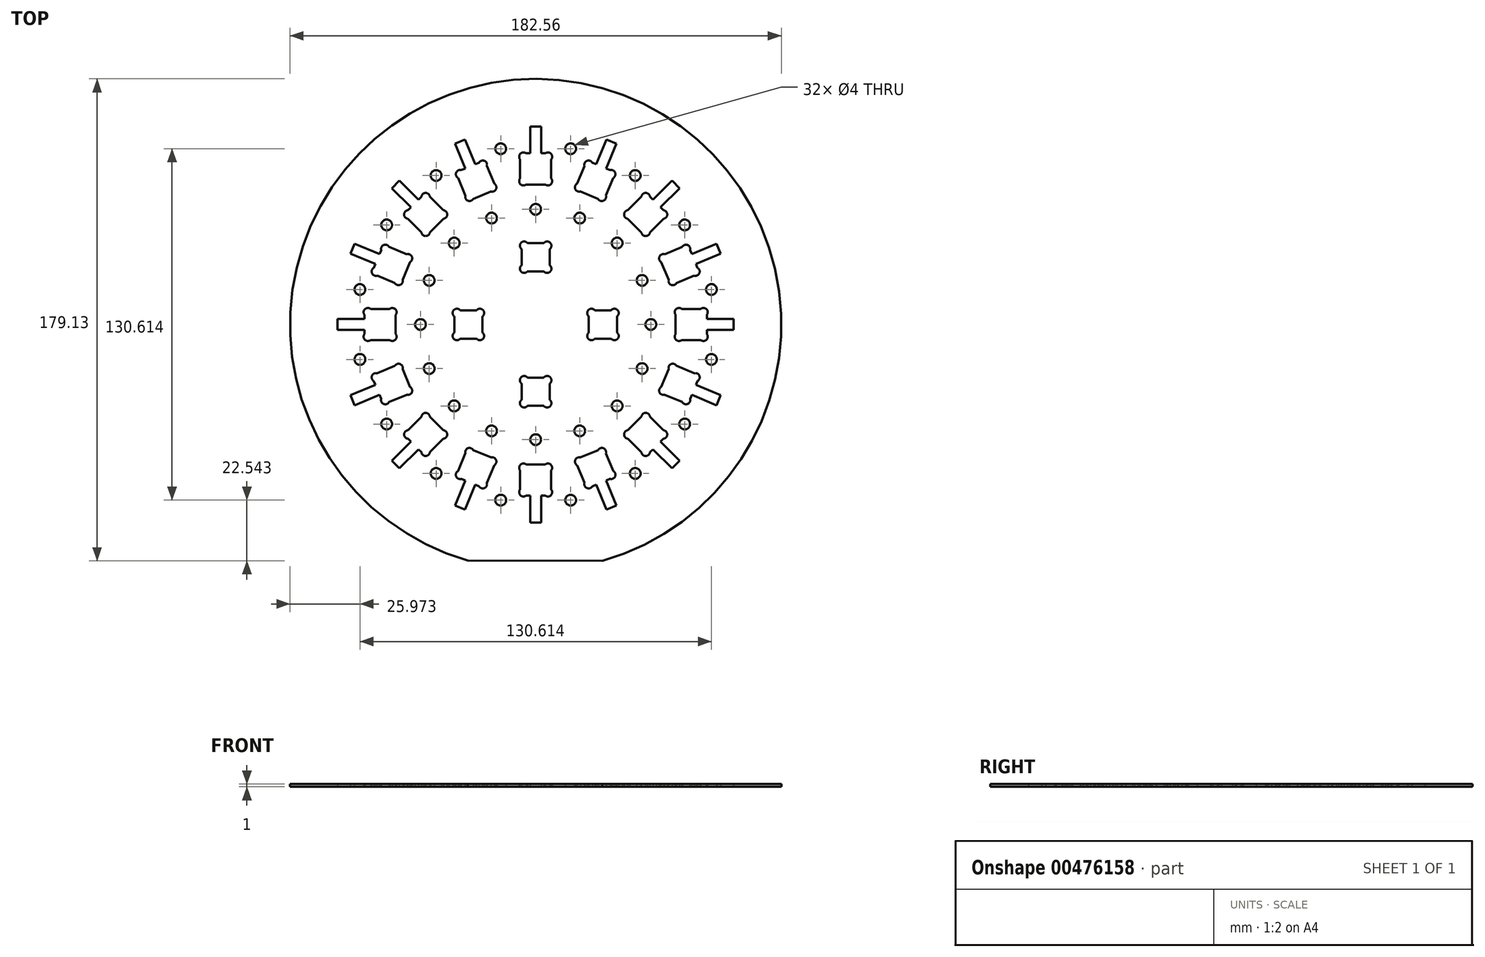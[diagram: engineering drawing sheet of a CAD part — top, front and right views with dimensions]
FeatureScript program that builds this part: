
annotation { "Feature Type Name" : "Feature", "Feature Type Description" : "" }
export const myFeature = defineFeature(function(context is Context, id is Id, definition is map)
    precondition{}
    {
        {
            var Q0;
            Q0=qCreatedBy(makeId("Top.planeOp"),FACE);
            var sketch = newSketch(context, id + "F0", { "sketchPlane" : qUnion([Q0])});
            skArc(sketch, "E0", {"start": v(24.78, -87.85) * mm, "mid": v(0.23, 91.28) * mm, "end": v(-25.22, -87.73) * mm});
            skLineSegment(sketch, "E1", {"start": v(-25.22, -87.73) * mm, "end": v(24.78, -87.85) * mm});
            skLineSegment(sketch, "E2", {"start": v(0, 0) * mm, "end": v(-0.22, -87.8) * mm, "construction": true});
            skLineSegment(sketch, "E3.bottom", {"start": v(5.8, 52) * mm, "end": v(3.57, 52) * mm, "construction": true});
            skLineSegment(sketch, "E3.top", {"start": v(5.8, 63.6) * mm, "end": v(3.57, 63.6) * mm, "construction": true});
            skLineSegment(sketch, "E3.left", {"start": v(5.8, 52) * mm, "end": v(5.8, 52) * mm});
            skLineSegment(sketch, "E3.right", {"start": v(-5.8, 52) * mm, "end": v(-5.8, 54.24) * mm, "construction": true});
            skPoint(sketch, "E3.middle", {"position": v(0, 57.8) * mm});
            skLineSegment(sketch, "E4", {"start": v(0, 57.8) * mm, "end": v(5.8, 63.6) * mm, "construction": true});
            skLineSegment(sketch, "E5", {"start": v(5.8, 63.6) * mm, "end": v(5.61, 63.54) * mm, "construction": true});
            skArc(sketch, "E6", {"start": v(5.8, 61.38) * mm, "mid": v(5.67, 63.48) * mm, "end": v(3.57, 63.6) * mm});
            skArc(sketch, "E7", {"start": v(3.57, 63.6) * mm, "mid": v(3.43, 61.23) * mm, "end": v(5.8, 61.38) * mm, "construction": true});
            skLineSegment(sketch, "E8", {"start": v(5.8, 61.38) * mm, "end": v(5.8, 63.6) * mm, "construction": true});
            skLineSegment(sketch, "E9", {"start": v(5.8, 52) * mm, "end": v(5.8, 54.24) * mm, "construction": true});
            skLineSegment(sketch, "E10", {"start": v(3.57, 63.6) * mm, "end": v(3.57, 63.6) * mm});
            skLineSegment(sketch, "E11", {"start": v(-5.8, 63.6) * mm, "end": v(-5.8, 63.6) * mm});
            skArc(sketch, "E12.1.0", {"start": v(-3.57, 63.6) * mm, "mid": v(-5.67, 63.48) * mm, "end": v(-5.8, 61.38) * mm});
            skArc(sketch, "E12.2.0", {"start": v(-5.8, 54.24) * mm, "mid": v(-5.67, 52.13) * mm, "end": v(-3.57, 52) * mm});
            skArc(sketch, "E13.2.3.0", {"start": v(3.57, 52) * mm, "mid": v(5.67, 52.13) * mm, "end": v(5.8, 54.24) * mm});
            skLineSegment(sketch, "E14", {"start": v(-5.8, 61.38) * mm, "end": v(-5.8, 63.6) * mm, "construction": true});
            skLineSegment(sketch, "E15", {"start": v(-5.8, 54.24) * mm, "end": v(-5.8, 61.38) * mm});
            skLineSegment(sketch, "E16", {"start": v(-3.57, 52) * mm, "end": v(-5.8, 52) * mm, "construction": true});
            skLineSegment(sketch, "E17", {"start": v(3.57, 52) * mm, "end": v(-3.57, 52) * mm});
            skLineSegment(sketch, "E18", {"start": v(3.57, 63.6) * mm, "end": v(-3.57, 63.6) * mm});
            skLineSegment(sketch, "E19", {"start": v(-3.57, 63.6) * mm, "end": v(-5.8, 63.6) * mm, "construction": true});
            skLineSegment(sketch, "E20", {"start": v(5.8, 54.24) * mm, "end": v(5.8, 61.38) * mm});
            skLineSegment(sketch, "E21", {"start": v(5.8, 61.38) * mm, "end": v(5.8, 61.38) * mm});
            skLineSegment(sketch, "E22", {"start": v(0, 57.8) * mm, "end": v(0, 42.8) * mm, "construction": true});
            skCircle(sketch, "E23", {"center": v(0, 42.8) * mm, "radius": 2 * mm});
            skCircle(sketch, "E24.1.0", {"center": v(13, 65.3) * mm, "radius": 2 * mm});
            skCircle(sketch, "E24.2.0", {"center": v(-13, 65.3) * mm, "radius": 2 * mm});
            skLineSegment(sketch, "E25.1.0", {"start": v(-26.11, 47.89) * mm, "end": v(-28.85, 54.49) * mm});
            skLineSegment(sketch, "E25.1.1", {"start": v(-16.6, 49.41) * mm, "end": v(-23.2, 46.68) * mm});
            skCircle(sketch, "E25.1.2", {"center": v(-16.38, 39.55) * mm, "radius": 2 * mm});
            skLineSegment(sketch, "E25.1.3", {"start": v(-22.12, 53.4) * mm, "end": v(-16.38, 39.55) * mm, "construction": true});
            skCircle(sketch, "E25.1.4", {"center": v(-37, 55.36) * mm, "radius": 2 * mm});
            skLineSegment(sketch, "E25.1.6", {"start": v(-15.4, 52.33) * mm, "end": v(-18.13, 58.93) * mm});
            skArc(sketch, "E25.1.7", {"start": v(-21.04, 60.13) * mm, "mid": v(-20.27, 57.89) * mm, "end": v(-18.13, 58.93) * mm, "construction": true});
            skPoint(sketch, "E25.1.8", {"position": v(-22.12, 53.4) * mm});
            skLineSegment(sketch, "E25.1.9", {"start": v(-22.12, 53.4) * mm, "end": v(-18.98, 60.98) * mm, "construction": true});
            skLineSegment(sketch, "E25.1.10", {"start": v(-21.04, 60.13) * mm, "end": v(-27.64, 57.4) * mm});
            skPoint(sketch, "E25.1.11", {"position": v(-22.12, 53.4) * mm});
            skArc(sketch, "E25.1.12", {"start": v(-26.11, 47.89) * mm, "mid": v(-25.2, 46) * mm, "end": v(-23.2, 46.68) * mm});
            skPoint(sketch, "E25.1.13", {"position": v(-22.12, 53.4) * mm});
            skLineSegment(sketch, "E25.1.14", {"start": v(-25.26, 45.83) * mm, "end": v(-26.11, 47.89) * mm, "construction": true});
            skLineSegment(sketch, "E25.1.15", {"start": v(-27.64, 57.4) * mm, "end": v(-29.7, 56.55) * mm, "construction": true});
            skArc(sketch, "E25.1.16", {"start": v(-27.64, 57.4) * mm, "mid": v(-29.53, 56.48) * mm, "end": v(-28.85, 54.49) * mm});
            skLineSegment(sketch, "E25.1.17", {"start": v(-14.54, 50.27) * mm, "end": v(-15.4, 52.33) * mm, "construction": true});
            skPoint(sketch, "E25.1.18", {"position": v(-22.12, 53.4) * mm});
            skLineSegment(sketch, "E25.1.19", {"start": v(-23.2, 46.68) * mm, "end": v(-25.26, 45.83) * mm, "construction": true});
            skArc(sketch, "E25.1.20", {"start": v(-16.6, 49.41) * mm, "mid": v(-14.7, 50.34) * mm, "end": v(-15.4, 52.33) * mm});
            skLineSegment(sketch, "E25.1.21", {"start": v(-14.54, 50.27) * mm, "end": v(-16.6, 49.41) * mm, "construction": true});
            skLineSegment(sketch, "E25.1.22", {"start": v(-28.85, 54.49) * mm, "end": v(-29.7, 56.55) * mm, "construction": true});
            skPoint(sketch, "E25.1.23", {"position": v(-22.12, 53.4) * mm});
            skPoint(sketch, "E25.1.24", {"position": v(-22.12, 53.4) * mm});
            skLineSegment(sketch, "E25.1.25", {"start": v(-18.13, 58.93) * mm, "end": v(-18.98, 60.98) * mm, "construction": true});
            skArc(sketch, "E25.1.26", {"start": v(-18.13, 58.93) * mm, "mid": v(-19.05, 60.82) * mm, "end": v(-21.04, 60.13) * mm});
            skLineSegment(sketch, "E25.1.27", {"start": v(-18.98, 60.98) * mm, "end": v(-19.13, 60.85) * mm, "construction": true});
            skLineSegment(sketch, "E25.1.28", {"start": v(-18.98, 60.98) * mm, "end": v(-21.04, 60.13) * mm, "construction": true});
            skLineSegment(sketch, "E25.2.0", {"start": v(-42.45, 34.25) * mm, "end": v(-47.5, 39.3) * mm});
            skLineSegment(sketch, "E25.2.1", {"start": v(-34.25, 39.3) * mm, "end": v(-39.3, 34.25) * mm});
            skCircle(sketch, "E25.2.2", {"center": v(-30.27, 30.27) * mm, "radius": 2 * mm});
            skLineSegment(sketch, "E25.2.3", {"start": v(-40.88, 40.88) * mm, "end": v(-30.27, 30.27) * mm, "construction": true});
            skCircle(sketch, "E25.2.4", {"center": v(-55.36, 37) * mm, "radius": 2 * mm});
            skCircle(sketch, "E25.2.5", {"center": v(-37, 55.36) * mm, "radius": 2 * mm});
            skLineSegment(sketch, "E25.2.6", {"start": v(-34.25, 42.45) * mm, "end": v(-39.3, 47.5) * mm});
            skArc(sketch, "E25.2.7", {"start": v(-42.45, 47.5) * mm, "mid": v(-40.88, 45.72) * mm, "end": v(-39.3, 47.5) * mm, "construction": true});
            skPoint(sketch, "E25.2.8", {"position": v(-40.88, 40.88) * mm});
            skLineSegment(sketch, "E25.2.9", {"start": v(-40.88, 40.88) * mm, "end": v(-40.88, 49.08) * mm, "construction": true});
            skLineSegment(sketch, "E25.2.10", {"start": v(-42.45, 47.5) * mm, "end": v(-47.5, 42.45) * mm});
            skPoint(sketch, "E25.2.11", {"position": v(-40.88, 40.88) * mm});
            skArc(sketch, "E25.2.12", {"start": v(-42.45, 34.25) * mm, "mid": v(-40.88, 32.85) * mm, "end": v(-39.3, 34.25) * mm});
            skPoint(sketch, "E25.2.13", {"position": v(-40.88, 40.88) * mm});
            skLineSegment(sketch, "E25.2.14", {"start": v(-40.88, 32.67) * mm, "end": v(-42.45, 34.25) * mm, "construction": true});
            skLineSegment(sketch, "E25.2.15", {"start": v(-47.5, 42.45) * mm, "end": v(-49.08, 40.88) * mm, "construction": true});
            skArc(sketch, "E25.2.16", {"start": v(-47.5, 42.45) * mm, "mid": v(-48.9, 40.88) * mm, "end": v(-47.5, 39.3) * mm});
            skLineSegment(sketch, "E25.2.17", {"start": v(-32.67, 40.88) * mm, "end": v(-34.25, 42.45) * mm, "construction": true});
            skPoint(sketch, "E25.2.18", {"position": v(-40.88, 40.88) * mm});
            skLineSegment(sketch, "E25.2.19", {"start": v(-39.3, 34.25) * mm, "end": v(-40.88, 32.67) * mm, "construction": true});
            skArc(sketch, "E25.2.20", {"start": v(-34.25, 39.3) * mm, "mid": v(-32.85, 40.88) * mm, "end": v(-34.25, 42.45) * mm});
            skLineSegment(sketch, "E25.2.21", {"start": v(-32.67, 40.88) * mm, "end": v(-34.25, 39.3) * mm, "construction": true});
            skLineSegment(sketch, "E25.2.22", {"start": v(-47.5, 39.3) * mm, "end": v(-49.08, 40.88) * mm, "construction": true});
            skPoint(sketch, "E25.2.23", {"position": v(-40.88, 40.88) * mm});
            skPoint(sketch, "E25.2.24", {"position": v(-40.88, 40.88) * mm});
            skLineSegment(sketch, "E25.2.25", {"start": v(-39.3, 47.5) * mm, "end": v(-40.88, 49.08) * mm, "construction": true});
            skArc(sketch, "E25.2.26", {"start": v(-39.3, 47.5) * mm, "mid": v(-40.88, 48.9) * mm, "end": v(-42.45, 47.5) * mm});
            skLineSegment(sketch, "E25.2.27", {"start": v(-40.88, 49.08) * mm, "end": v(-40.96, 48.9) * mm, "construction": true});
            skLineSegment(sketch, "E25.2.28", {"start": v(-40.88, 49.08) * mm, "end": v(-42.45, 47.5) * mm, "construction": true});
            skLineSegment(sketch, "E26.3.3.0", {"start": v(-46.68, 23.2) * mm, "end": v(-49.41, 16.6) * mm});
            skCircle(sketch, "E26.6.3.0", {"center": v(-39.55, 16.38) * mm, "radius": 2 * mm});
            skLineSegment(sketch, "E26.7.3.0", {"start": v(-52.33, 15.4) * mm, "end": v(-58.93, 18.13) * mm});
            skLineSegment(sketch, "E26.8.3.0", {"start": v(-53.4, 22.12) * mm, "end": v(-39.55, 16.38) * mm, "construction": true});
            skCircle(sketch, "E26.11.3.0", {"center": v(-65.3, 13) * mm, "radius": 2 * mm});
            skLineSegment(sketch, "E26.15.3.0", {"start": v(-47.89, 26.11) * mm, "end": v(-54.49, 28.85) * mm});
            skArc(sketch, "E26.18.3.0", {"start": v(-57.4, 27.64) * mm, "mid": v(-55.26, 26.6) * mm, "end": v(-54.49, 28.85) * mm, "construction": true});
            skPoint(sketch, "E26.22.3.0", {"position": v(-53.4, 22.12) * mm});
            skLineSegment(sketch, "E26.23.3.0", {"start": v(-53.4, 22.12) * mm, "end": v(-56.55, 29.7) * mm, "construction": true});
            skLineSegment(sketch, "E26.26.3.0", {"start": v(-57.4, 27.64) * mm, "end": v(-60.13, 21.04) * mm});
            skPoint(sketch, "E26.29.3.0", {"position": v(-53.4, 22.12) * mm});
            skArc(sketch, "E26.30.3.0", {"start": v(-52.33, 15.4) * mm, "mid": v(-50.34, 14.7) * mm, "end": v(-49.41, 16.6) * mm});
            skPoint(sketch, "E26.34.3.0", {"position": v(-53.4, 22.12) * mm});
            skLineSegment(sketch, "E26.35.3.0", {"start": v(-50.27, 14.54) * mm, "end": v(-52.33, 15.4) * mm, "construction": true});
            skLineSegment(sketch, "E26.38.3.0", {"start": v(-60.13, 21.04) * mm, "end": v(-60.98, 18.98) * mm, "construction": true});
            skArc(sketch, "E26.41.3.0", {"start": v(-60.13, 21.04) * mm, "mid": v(-60.82, 19.05) * mm, "end": v(-58.93, 18.13) * mm});
            skLineSegment(sketch, "E26.45.3.0", {"start": v(-45.83, 25.26) * mm, "end": v(-47.89, 26.11) * mm, "construction": true});
            skPoint(sketch, "E26.48.3.0", {"position": v(-53.4, 22.12) * mm});
            skLineSegment(sketch, "E26.49.3.0", {"start": v(-49.41, 16.6) * mm, "end": v(-50.27, 14.54) * mm, "construction": true});
            skArc(sketch, "E26.52.3.0", {"start": v(-46.68, 23.2) * mm, "mid": v(-46, 25.2) * mm, "end": v(-47.89, 26.11) * mm});
            skLineSegment(sketch, "E26.56.3.0", {"start": v(-45.83, 25.26) * mm, "end": v(-46.68, 23.2) * mm, "construction": true});
            skLineSegment(sketch, "E26.59.3.0", {"start": v(-58.93, 18.13) * mm, "end": v(-60.98, 18.98) * mm, "construction": true});
            skPoint(sketch, "E26.62.3.0", {"position": v(-53.4, 22.12) * mm});
            skPoint(sketch, "E26.63.3.0", {"position": v(-53.4, 22.12) * mm});
            skLineSegment(sketch, "E26.64.3.0", {"start": v(-54.49, 28.85) * mm, "end": v(-56.55, 29.7) * mm, "construction": true});
            skArc(sketch, "E26.67.3.0", {"start": v(-54.49, 28.85) * mm, "mid": v(-56.48, 29.53) * mm, "end": v(-57.4, 27.64) * mm});
            skLineSegment(sketch, "E26.71.3.0", {"start": v(-56.55, 29.7) * mm, "end": v(-56.55, 29.5) * mm, "construction": true});
            skLineSegment(sketch, "E26.74.3.0", {"start": v(-56.55, 29.7) * mm, "end": v(-57.4, 27.64) * mm, "construction": true});
            skLineSegment(sketch, "E26.3.4.0", {"start": v(-52, 3.57) * mm, "end": v(-52, -3.57) * mm});
            skCircle(sketch, "E26.6.4.0", {"center": v(-42.8, 0) * mm, "radius": 2 * mm});
            skLineSegment(sketch, "E26.7.4.0", {"start": v(-54.24, -5.8) * mm, "end": v(-61.38, -5.8) * mm});
            skLineSegment(sketch, "E26.8.4.0", {"start": v(-57.8, 0) * mm, "end": v(-42.8, 0) * mm, "construction": true});
            skCircle(sketch, "E26.11.4.0", {"center": v(-65.3, -13) * mm, "radius": 2 * mm});
            skCircle(sketch, "E26.13.4.0", {"center": v(-65.3, 13) * mm, "radius": 2 * mm});
            skLineSegment(sketch, "E26.15.4.0", {"start": v(-54.24, 5.8) * mm, "end": v(-61.38, 5.8) * mm});
            skArc(sketch, "E26.18.4.0", {"start": v(-63.6, 3.57) * mm, "mid": v(-61.23, 3.43) * mm, "end": v(-61.38, 5.8) * mm, "construction": true});
            skPoint(sketch, "E26.22.4.0", {"position": v(-57.8, 0) * mm});
            skLineSegment(sketch, "E26.23.4.0", {"start": v(-57.8, 0) * mm, "end": v(-63.6, 5.8) * mm, "construction": true});
            skLineSegment(sketch, "E26.26.4.0", {"start": v(-63.6, 3.57) * mm, "end": v(-63.6, -3.57) * mm});
            skPoint(sketch, "E26.29.4.0", {"position": v(-57.8, 0) * mm});
            skArc(sketch, "E26.30.4.0", {"start": v(-54.24, -5.8) * mm, "mid": v(-52.13, -5.67) * mm, "end": v(-52, -3.57) * mm});
            skPoint(sketch, "E26.34.4.0", {"position": v(-57.8, 0) * mm});
            skLineSegment(sketch, "E26.35.4.0", {"start": v(-52, -5.8) * mm, "end": v(-54.24, -5.8) * mm, "construction": true});
            skLineSegment(sketch, "E26.38.4.0", {"start": v(-63.6, -3.57) * mm, "end": v(-63.6, -5.8) * mm, "construction": true});
            skArc(sketch, "E26.41.4.0", {"start": v(-63.6, -3.57) * mm, "mid": v(-63.48, -5.67) * mm, "end": v(-61.38, -5.8) * mm});
            skLineSegment(sketch, "E26.45.4.0", {"start": v(-52, 5.8) * mm, "end": v(-54.24, 5.8) * mm, "construction": true});
            skPoint(sketch, "E26.48.4.0", {"position": v(-57.8, 0) * mm});
            skLineSegment(sketch, "E26.49.4.0", {"start": v(-52, -3.57) * mm, "end": v(-52, -5.8) * mm, "construction": true});
            skArc(sketch, "E26.52.4.0", {"start": v(-52, 3.57) * mm, "mid": v(-52.13, 5.67) * mm, "end": v(-54.24, 5.8) * mm});
            skLineSegment(sketch, "E26.56.4.0", {"start": v(-52, 5.8) * mm, "end": v(-52, 3.57) * mm, "construction": true});
            skLineSegment(sketch, "E26.59.4.0", {"start": v(-61.38, -5.8) * mm, "end": v(-63.6, -5.8) * mm, "construction": true});
            skPoint(sketch, "E26.62.4.0", {"position": v(-57.8, 0) * mm});
            skPoint(sketch, "E26.63.4.0", {"position": v(-57.8, 0) * mm});
            skLineSegment(sketch, "E26.64.4.0", {"start": v(-61.38, 5.8) * mm, "end": v(-63.6, 5.8) * mm, "construction": true});
            skArc(sketch, "E26.67.4.0", {"start": v(-61.38, 5.8) * mm, "mid": v(-63.48, 5.67) * mm, "end": v(-63.6, 3.57) * mm});
            skLineSegment(sketch, "E26.71.4.0", {"start": v(-63.6, 5.8) * mm, "end": v(-63.54, 5.61) * mm, "construction": true});
            skLineSegment(sketch, "E26.74.4.0", {"start": v(-63.6, 5.8) * mm, "end": v(-63.6, 3.57) * mm, "construction": true});
            skLineSegment(sketch, "E27.3.5.0", {"start": v(-49.41, -16.6) * mm, "end": v(-46.68, -23.2) * mm});
            skCircle(sketch, "E27.6.5.0", {"center": v(-39.55, -16.38) * mm, "radius": 2 * mm});
            skLineSegment(sketch, "E27.7.5.0", {"start": v(-47.89, -26.11) * mm, "end": v(-54.49, -28.85) * mm});
            skLineSegment(sketch, "E27.8.5.0", {"start": v(-53.4, -22.12) * mm, "end": v(-39.55, -16.38) * mm, "construction": true});
            skCircle(sketch, "E27.11.5.0", {"center": v(-55.36, -37) * mm, "radius": 2 * mm});
            skLineSegment(sketch, "E27.15.5.0", {"start": v(-52.33, -15.4) * mm, "end": v(-58.93, -18.13) * mm});
            skArc(sketch, "E27.18.5.0", {"start": v(-60.13, -21.04) * mm, "mid": v(-57.89, -20.27) * mm, "end": v(-58.93, -18.13) * mm, "construction": true});
            skPoint(sketch, "E27.22.5.0", {"position": v(-53.4, -22.12) * mm});
            skLineSegment(sketch, "E27.23.5.0", {"start": v(-53.4, -22.12) * mm, "end": v(-60.98, -18.98) * mm, "construction": true});
            skLineSegment(sketch, "E27.26.5.0", {"start": v(-60.13, -21.04) * mm, "end": v(-57.4, -27.64) * mm});
            skPoint(sketch, "E27.29.5.0", {"position": v(-53.4, -22.12) * mm});
            skArc(sketch, "E27.30.5.0", {"start": v(-47.89, -26.11) * mm, "mid": v(-46, -25.2) * mm, "end": v(-46.68, -23.2) * mm});
            skPoint(sketch, "E27.34.5.0", {"position": v(-53.4, -22.12) * mm});
            skLineSegment(sketch, "E27.35.5.0", {"start": v(-45.83, -25.26) * mm, "end": v(-47.89, -26.11) * mm, "construction": true});
            skLineSegment(sketch, "E27.38.5.0", {"start": v(-57.4, -27.64) * mm, "end": v(-56.55, -29.7) * mm, "construction": true});
            skArc(sketch, "E27.41.5.0", {"start": v(-57.4, -27.64) * mm, "mid": v(-56.48, -29.53) * mm, "end": v(-54.49, -28.85) * mm});
            skLineSegment(sketch, "E27.45.5.0", {"start": v(-50.27, -14.54) * mm, "end": v(-52.33, -15.4) * mm, "construction": true});
            skPoint(sketch, "E27.48.5.0", {"position": v(-53.4, -22.12) * mm});
            skLineSegment(sketch, "E27.49.5.0", {"start": v(-46.68, -23.2) * mm, "end": v(-45.83, -25.26) * mm, "construction": true});
            skArc(sketch, "E27.52.5.0", {"start": v(-49.41, -16.6) * mm, "mid": v(-50.34, -14.7) * mm, "end": v(-52.33, -15.4) * mm});
            skLineSegment(sketch, "E27.56.5.0", {"start": v(-50.27, -14.54) * mm, "end": v(-49.41, -16.6) * mm, "construction": true});
            skLineSegment(sketch, "E27.59.5.0", {"start": v(-54.49, -28.85) * mm, "end": v(-56.55, -29.7) * mm, "construction": true});
            skPoint(sketch, "E27.62.5.0", {"position": v(-53.4, -22.12) * mm});
            skPoint(sketch, "E27.63.5.0", {"position": v(-53.4, -22.12) * mm});
            skLineSegment(sketch, "E27.64.5.0", {"start": v(-58.93, -18.13) * mm, "end": v(-60.98, -18.98) * mm, "construction": true});
            skArc(sketch, "E27.67.5.0", {"start": v(-58.93, -18.13) * mm, "mid": v(-60.82, -19.05) * mm, "end": v(-60.13, -21.04) * mm});
            skLineSegment(sketch, "E27.71.5.0", {"start": v(-60.98, -18.98) * mm, "end": v(-60.85, -19.13) * mm, "construction": true});
            skLineSegment(sketch, "E27.74.5.0", {"start": v(-60.98, -18.98) * mm, "end": v(-60.13, -21.04) * mm, "construction": true});
            skLineSegment(sketch, "E27.3.6.0", {"start": v(-39.3, -34.25) * mm, "end": v(-34.25, -39.3) * mm});
            skCircle(sketch, "E27.6.6.0", {"center": v(-30.27, -30.27) * mm, "radius": 2 * mm});
            skLineSegment(sketch, "E27.7.6.0", {"start": v(-34.25, -42.45) * mm, "end": v(-39.3, -47.5) * mm});
            skLineSegment(sketch, "E27.8.6.0", {"start": v(-40.88, -40.88) * mm, "end": v(-30.27, -30.27) * mm, "construction": true});
            skCircle(sketch, "E27.11.6.0", {"center": v(-37, -55.36) * mm, "radius": 2 * mm});
            skCircle(sketch, "E27.13.6.0", {"center": v(-55.36, -37) * mm, "radius": 2 * mm});
            skLineSegment(sketch, "E27.15.6.0", {"start": v(-42.45, -34.25) * mm, "end": v(-47.5, -39.3) * mm});
            skArc(sketch, "E27.18.6.0", {"start": v(-47.5, -42.45) * mm, "mid": v(-45.72, -40.88) * mm, "end": v(-47.5, -39.3) * mm, "construction": true});
            skPoint(sketch, "E27.22.6.0", {"position": v(-40.88, -40.88) * mm});
            skLineSegment(sketch, "E27.23.6.0", {"start": v(-40.88, -40.88) * mm, "end": v(-49.08, -40.88) * mm, "construction": true});
            skLineSegment(sketch, "E27.26.6.0", {"start": v(-47.5, -42.45) * mm, "end": v(-42.45, -47.5) * mm});
            skPoint(sketch, "E27.29.6.0", {"position": v(-40.88, -40.88) * mm});
            skArc(sketch, "E27.30.6.0", {"start": v(-34.25, -42.45) * mm, "mid": v(-32.85, -40.88) * mm, "end": v(-34.25, -39.3) * mm});
            skPoint(sketch, "E27.34.6.0", {"position": v(-40.88, -40.88) * mm});
            skLineSegment(sketch, "E27.35.6.0", {"start": v(-32.67, -40.88) * mm, "end": v(-34.25, -42.45) * mm, "construction": true});
            skLineSegment(sketch, "E27.38.6.0", {"start": v(-42.45, -47.5) * mm, "end": v(-40.88, -49.08) * mm, "construction": true});
            skArc(sketch, "E27.41.6.0", {"start": v(-42.45, -47.5) * mm, "mid": v(-40.88, -48.9) * mm, "end": v(-39.3, -47.5) * mm});
            skLineSegment(sketch, "E27.45.6.0", {"start": v(-40.88, -32.67) * mm, "end": v(-42.45, -34.25) * mm, "construction": true});
            skPoint(sketch, "E27.48.6.0", {"position": v(-40.88, -40.88) * mm});
            skLineSegment(sketch, "E27.49.6.0", {"start": v(-34.25, -39.3) * mm, "end": v(-32.67, -40.88) * mm, "construction": true});
            skArc(sketch, "E27.52.6.0", {"start": v(-39.3, -34.25) * mm, "mid": v(-40.88, -32.85) * mm, "end": v(-42.45, -34.25) * mm});
            skLineSegment(sketch, "E27.56.6.0", {"start": v(-40.88, -32.67) * mm, "end": v(-39.3, -34.25) * mm, "construction": true});
            skLineSegment(sketch, "E27.59.6.0", {"start": v(-39.3, -47.5) * mm, "end": v(-40.88, -49.08) * mm, "construction": true});
            skPoint(sketch, "E27.62.6.0", {"position": v(-40.88, -40.88) * mm});
            skPoint(sketch, "E27.63.6.0", {"position": v(-40.88, -40.88) * mm});
            skLineSegment(sketch, "E27.64.6.0", {"start": v(-47.5, -39.3) * mm, "end": v(-49.08, -40.88) * mm, "construction": true});
            skArc(sketch, "E27.67.6.0", {"start": v(-47.5, -39.3) * mm, "mid": v(-48.9, -40.88) * mm, "end": v(-47.5, -42.45) * mm});
            skLineSegment(sketch, "E27.71.6.0", {"start": v(-49.08, -40.88) * mm, "end": v(-48.9, -40.96) * mm, "construction": true});
            skLineSegment(sketch, "E27.74.6.0", {"start": v(-49.08, -40.88) * mm, "end": v(-47.5, -42.45) * mm, "construction": true});
            skLineSegment(sketch, "E27.3.7.0", {"start": v(-23.2, -46.68) * mm, "end": v(-16.6, -49.41) * mm});
            skCircle(sketch, "E27.6.7.0", {"center": v(-16.38, -39.55) * mm, "radius": 2 * mm});
            skLineSegment(sketch, "E27.7.7.0", {"start": v(-15.4, -52.33) * mm, "end": v(-18.13, -58.93) * mm});
            skLineSegment(sketch, "E27.8.7.0", {"start": v(-22.12, -53.4) * mm, "end": v(-16.38, -39.55) * mm, "construction": true});
            skCircle(sketch, "E27.11.7.0", {"center": v(-13, -65.3) * mm, "radius": 2 * mm});
            skCircle(sketch, "E27.13.7.0", {"center": v(-37, -55.36) * mm, "radius": 2 * mm});
            skLineSegment(sketch, "E27.15.7.0", {"start": v(-26.11, -47.89) * mm, "end": v(-28.85, -54.49) * mm});
            skArc(sketch, "E27.18.7.0", {"start": v(-27.64, -57.4) * mm, "mid": v(-26.6, -55.26) * mm, "end": v(-28.85, -54.49) * mm, "construction": true});
            skPoint(sketch, "E27.22.7.0", {"position": v(-22.12, -53.4) * mm});
            skLineSegment(sketch, "E27.23.7.0", {"start": v(-22.12, -53.4) * mm, "end": v(-29.7, -56.55) * mm, "construction": true});
            skLineSegment(sketch, "E27.26.7.0", {"start": v(-27.64, -57.4) * mm, "end": v(-21.04, -60.13) * mm});
            skPoint(sketch, "E27.29.7.0", {"position": v(-22.12, -53.4) * mm});
            skArc(sketch, "E27.30.7.0", {"start": v(-15.4, -52.33) * mm, "mid": v(-14.7, -50.34) * mm, "end": v(-16.6, -49.41) * mm});
            skPoint(sketch, "E27.34.7.0", {"position": v(-22.12, -53.4) * mm});
            skLineSegment(sketch, "E27.35.7.0", {"start": v(-14.54, -50.27) * mm, "end": v(-15.4, -52.33) * mm, "construction": true});
            skLineSegment(sketch, "E27.38.7.0", {"start": v(-21.04, -60.13) * mm, "end": v(-18.98, -60.98) * mm, "construction": true});
            skArc(sketch, "E27.41.7.0", {"start": v(-21.04, -60.13) * mm, "mid": v(-19.05, -60.82) * mm, "end": v(-18.13, -58.93) * mm});
            skLineSegment(sketch, "E27.45.7.0", {"start": v(-25.26, -45.83) * mm, "end": v(-26.11, -47.89) * mm, "construction": true});
            skPoint(sketch, "E27.48.7.0", {"position": v(-22.12, -53.4) * mm});
            skLineSegment(sketch, "E27.49.7.0", {"start": v(-16.6, -49.41) * mm, "end": v(-14.54, -50.27) * mm, "construction": true});
            skArc(sketch, "E27.52.7.0", {"start": v(-23.2, -46.68) * mm, "mid": v(-25.2, -46) * mm, "end": v(-26.11, -47.89) * mm});
            skLineSegment(sketch, "E27.56.7.0", {"start": v(-25.26, -45.83) * mm, "end": v(-23.2, -46.68) * mm, "construction": true});
            skLineSegment(sketch, "E27.59.7.0", {"start": v(-18.13, -58.93) * mm, "end": v(-18.98, -60.98) * mm, "construction": true});
            skPoint(sketch, "E27.62.7.0", {"position": v(-22.12, -53.4) * mm});
            skPoint(sketch, "E27.63.7.0", {"position": v(-22.12, -53.4) * mm});
            skLineSegment(sketch, "E27.64.7.0", {"start": v(-28.85, -54.49) * mm, "end": v(-29.7, -56.55) * mm, "construction": true});
            skArc(sketch, "E27.67.7.0", {"start": v(-28.85, -54.49) * mm, "mid": v(-29.53, -56.48) * mm, "end": v(-27.64, -57.4) * mm});
            skLineSegment(sketch, "E27.71.7.0", {"start": v(-29.7, -56.55) * mm, "end": v(-29.5, -56.55) * mm, "construction": true});
            skLineSegment(sketch, "E27.74.7.0", {"start": v(-29.7, -56.55) * mm, "end": v(-27.64, -57.4) * mm, "construction": true});
            skLineSegment(sketch, "E27.3.8.0", {"start": v(-3.57, -52) * mm, "end": v(3.57, -52) * mm});
            skCircle(sketch, "E27.6.8.0", {"center": v(0, -42.8) * mm, "radius": 2 * mm});
            skLineSegment(sketch, "E27.7.8.0", {"start": v(5.8, -54.24) * mm, "end": v(5.8, -61.38) * mm});
            skLineSegment(sketch, "E27.8.8.0", {"start": v(0, -57.8) * mm, "end": v(0, -42.8) * mm, "construction": true});
            skCircle(sketch, "E27.11.8.0", {"center": v(13, -65.3) * mm, "radius": 2 * mm});
            skCircle(sketch, "E27.13.8.0", {"center": v(-13, -65.3) * mm, "radius": 2 * mm});
            skLineSegment(sketch, "E27.15.8.0", {"start": v(-5.8, -54.24) * mm, "end": v(-5.8, -61.38) * mm});
            skArc(sketch, "E27.18.8.0", {"start": v(-3.57, -63.6) * mm, "mid": v(-3.43, -61.23) * mm, "end": v(-5.8, -61.38) * mm, "construction": true});
            skPoint(sketch, "E27.22.8.0", {"position": v(0, -57.8) * mm});
            skLineSegment(sketch, "E27.23.8.0", {"start": v(0, -57.8) * mm, "end": v(-5.8, -63.6) * mm, "construction": true});
            skLineSegment(sketch, "E27.26.8.0", {"start": v(-3.57, -63.6) * mm, "end": v(3.57, -63.6) * mm});
            skPoint(sketch, "E27.29.8.0", {"position": v(0, -57.8) * mm});
            skArc(sketch, "E27.30.8.0", {"start": v(5.8, -54.24) * mm, "mid": v(5.67, -52.13) * mm, "end": v(3.57, -52) * mm});
            skPoint(sketch, "E27.34.8.0", {"position": v(0, -57.8) * mm});
            skLineSegment(sketch, "E27.35.8.0", {"start": v(5.8, -52) * mm, "end": v(5.8, -54.24) * mm, "construction": true});
            skLineSegment(sketch, "E27.38.8.0", {"start": v(3.57, -63.6) * mm, "end": v(5.8, -63.6) * mm, "construction": true});
            skArc(sketch, "E27.41.8.0", {"start": v(3.57, -63.6) * mm, "mid": v(5.67, -63.48) * mm, "end": v(5.8, -61.38) * mm});
            skLineSegment(sketch, "E27.45.8.0", {"start": v(-5.8, -52) * mm, "end": v(-5.8, -54.24) * mm, "construction": true});
            skPoint(sketch, "E27.48.8.0", {"position": v(0, -57.8) * mm});
            skLineSegment(sketch, "E27.49.8.0", {"start": v(3.57, -52) * mm, "end": v(5.8, -52) * mm, "construction": true});
            skArc(sketch, "E27.52.8.0", {"start": v(-3.57, -52) * mm, "mid": v(-5.67, -52.13) * mm, "end": v(-5.8, -54.24) * mm});
            skLineSegment(sketch, "E27.56.8.0", {"start": v(-5.8, -52) * mm, "end": v(-3.57, -52) * mm, "construction": true});
            skLineSegment(sketch, "E27.59.8.0", {"start": v(5.8, -61.38) * mm, "end": v(5.8, -63.6) * mm, "construction": true});
            skPoint(sketch, "E27.62.8.0", {"position": v(0, -57.8) * mm});
            skPoint(sketch, "E27.63.8.0", {"position": v(0, -57.8) * mm});
            skLineSegment(sketch, "E27.64.8.0", {"start": v(-5.8, -61.38) * mm, "end": v(-5.8, -63.6) * mm, "construction": true});
            skArc(sketch, "E27.67.8.0", {"start": v(-5.8, -61.38) * mm, "mid": v(-5.67, -63.48) * mm, "end": v(-3.57, -63.6) * mm});
            skLineSegment(sketch, "E27.71.8.0", {"start": v(-5.8, -63.6) * mm, "end": v(-5.61, -63.54) * mm, "construction": true});
            skLineSegment(sketch, "E27.74.8.0", {"start": v(-5.8, -63.6) * mm, "end": v(-3.57, -63.6) * mm, "construction": true});
            skLineSegment(sketch, "E27.3.9.0", {"start": v(16.6, -49.41) * mm, "end": v(23.2, -46.68) * mm});
            skCircle(sketch, "E27.6.9.0", {"center": v(16.38, -39.55) * mm, "radius": 2 * mm});
            skLineSegment(sketch, "E27.7.9.0", {"start": v(26.11, -47.89) * mm, "end": v(28.85, -54.49) * mm});
            skLineSegment(sketch, "E27.8.9.0", {"start": v(22.12, -53.4) * mm, "end": v(16.38, -39.55) * mm, "construction": true});
            skCircle(sketch, "E27.11.9.0", {"center": v(37, -55.36) * mm, "radius": 2 * mm});
            skCircle(sketch, "E27.13.9.0", {"center": v(13, -65.3) * mm, "radius": 2 * mm});
            skLineSegment(sketch, "E27.15.9.0", {"start": v(15.4, -52.33) * mm, "end": v(18.13, -58.93) * mm});
            skArc(sketch, "E27.18.9.0", {"start": v(21.04, -60.13) * mm, "mid": v(20.27, -57.89) * mm, "end": v(18.13, -58.93) * mm, "construction": true});
            skPoint(sketch, "E27.22.9.0", {"position": v(22.12, -53.4) * mm});
            skLineSegment(sketch, "E27.23.9.0", {"start": v(22.12, -53.4) * mm, "end": v(18.98, -60.98) * mm, "construction": true});
            skLineSegment(sketch, "E27.26.9.0", {"start": v(21.04, -60.13) * mm, "end": v(27.64, -57.4) * mm});
            skPoint(sketch, "E27.29.9.0", {"position": v(22.12, -53.4) * mm});
            skArc(sketch, "E27.30.9.0", {"start": v(26.11, -47.89) * mm, "mid": v(25.2, -46) * mm, "end": v(23.2, -46.68) * mm});
            skPoint(sketch, "E27.34.9.0", {"position": v(22.12, -53.4) * mm});
            skLineSegment(sketch, "E27.35.9.0", {"start": v(25.26, -45.83) * mm, "end": v(26.11, -47.89) * mm, "construction": true});
            skLineSegment(sketch, "E27.38.9.0", {"start": v(27.64, -57.4) * mm, "end": v(29.7, -56.55) * mm, "construction": true});
            skArc(sketch, "E27.41.9.0", {"start": v(27.64, -57.4) * mm, "mid": v(29.53, -56.48) * mm, "end": v(28.85, -54.49) * mm});
            skLineSegment(sketch, "E27.45.9.0", {"start": v(14.54, -50.27) * mm, "end": v(15.4, -52.33) * mm, "construction": true});
            skPoint(sketch, "E27.48.9.0", {"position": v(22.12, -53.4) * mm});
            skLineSegment(sketch, "E27.49.9.0", {"start": v(23.2, -46.68) * mm, "end": v(25.26, -45.83) * mm, "construction": true});
            skArc(sketch, "E27.52.9.0", {"start": v(16.6, -49.41) * mm, "mid": v(14.7, -50.34) * mm, "end": v(15.4, -52.33) * mm});
            skLineSegment(sketch, "E27.56.9.0", {"start": v(14.54, -50.27) * mm, "end": v(16.6, -49.41) * mm, "construction": true});
            skLineSegment(sketch, "E27.59.9.0", {"start": v(28.85, -54.49) * mm, "end": v(29.7, -56.55) * mm, "construction": true});
            skPoint(sketch, "E27.62.9.0", {"position": v(22.12, -53.4) * mm});
            skPoint(sketch, "E27.63.9.0", {"position": v(22.12, -53.4) * mm});
            skLineSegment(sketch, "E27.64.9.0", {"start": v(18.13, -58.93) * mm, "end": v(18.98, -60.98) * mm, "construction": true});
            skArc(sketch, "E27.67.9.0", {"start": v(18.13, -58.93) * mm, "mid": v(19.05, -60.82) * mm, "end": v(21.04, -60.13) * mm});
            skLineSegment(sketch, "E27.71.9.0", {"start": v(18.98, -60.98) * mm, "end": v(19.13, -60.85) * mm, "construction": true});
            skLineSegment(sketch, "E27.74.9.0", {"start": v(18.98, -60.98) * mm, "end": v(21.04, -60.13) * mm, "construction": true});
            skLineSegment(sketch, "E27.3.10.0", {"start": v(34.25, -39.3) * mm, "end": v(39.3, -34.25) * mm});
            skCircle(sketch, "E27.6.10.0", {"center": v(30.27, -30.27) * mm, "radius": 2 * mm});
            skLineSegment(sketch, "E27.7.10.0", {"start": v(42.45, -34.25) * mm, "end": v(47.5, -39.3) * mm});
            skLineSegment(sketch, "E27.8.10.0", {"start": v(40.88, -40.88) * mm, "end": v(30.27, -30.27) * mm, "construction": true});
            skCircle(sketch, "E27.11.10.0", {"center": v(55.36, -37) * mm, "radius": 2 * mm});
            skCircle(sketch, "E27.13.10.0", {"center": v(37, -55.36) * mm, "radius": 2 * mm});
            skLineSegment(sketch, "E27.15.10.0", {"start": v(34.25, -42.45) * mm, "end": v(39.3, -47.5) * mm});
            skArc(sketch, "E27.18.10.0", {"start": v(42.45, -47.5) * mm, "mid": v(40.88, -45.72) * mm, "end": v(39.3, -47.5) * mm, "construction": true});
            skPoint(sketch, "E27.22.10.0", {"position": v(40.88, -40.88) * mm});
            skLineSegment(sketch, "E27.23.10.0", {"start": v(40.88, -40.88) * mm, "end": v(40.88, -49.08) * mm, "construction": true});
            skLineSegment(sketch, "E27.26.10.0", {"start": v(42.45, -47.5) * mm, "end": v(47.5, -42.45) * mm});
            skPoint(sketch, "E27.29.10.0", {"position": v(40.88, -40.88) * mm});
            skArc(sketch, "E27.30.10.0", {"start": v(42.45, -34.25) * mm, "mid": v(40.88, -32.85) * mm, "end": v(39.3, -34.25) * mm});
            skPoint(sketch, "E27.34.10.0", {"position": v(40.88, -40.88) * mm});
            skLineSegment(sketch, "E27.35.10.0", {"start": v(40.88, -32.67) * mm, "end": v(42.45, -34.25) * mm, "construction": true});
            skLineSegment(sketch, "E27.38.10.0", {"start": v(47.5, -42.45) * mm, "end": v(49.08, -40.88) * mm, "construction": true});
            skArc(sketch, "E27.41.10.0", {"start": v(47.5, -42.45) * mm, "mid": v(48.9, -40.88) * mm, "end": v(47.5, -39.3) * mm});
            skLineSegment(sketch, "E27.45.10.0", {"start": v(32.67, -40.88) * mm, "end": v(34.25, -42.45) * mm, "construction": true});
            skPoint(sketch, "E27.48.10.0", {"position": v(40.88, -40.88) * mm});
            skLineSegment(sketch, "E27.49.10.0", {"start": v(39.3, -34.25) * mm, "end": v(40.88, -32.67) * mm, "construction": true});
            skArc(sketch, "E27.52.10.0", {"start": v(34.25, -39.3) * mm, "mid": v(32.85, -40.88) * mm, "end": v(34.25, -42.45) * mm});
            skLineSegment(sketch, "E27.56.10.0", {"start": v(32.67, -40.88) * mm, "end": v(34.25, -39.3) * mm, "construction": true});
            skLineSegment(sketch, "E27.59.10.0", {"start": v(47.5, -39.3) * mm, "end": v(49.08, -40.88) * mm, "construction": true});
            skPoint(sketch, "E27.62.10.0", {"position": v(40.88, -40.88) * mm});
            skPoint(sketch, "E27.63.10.0", {"position": v(40.88, -40.88) * mm});
            skLineSegment(sketch, "E27.64.10.0", {"start": v(39.3, -47.5) * mm, "end": v(40.88, -49.08) * mm, "construction": true});
            skArc(sketch, "E27.67.10.0", {"start": v(39.3, -47.5) * mm, "mid": v(40.88, -48.9) * mm, "end": v(42.45, -47.5) * mm});
            skLineSegment(sketch, "E27.71.10.0", {"start": v(40.88, -49.08) * mm, "end": v(40.96, -48.9) * mm, "construction": true});
            skLineSegment(sketch, "E27.74.10.0", {"start": v(40.88, -49.08) * mm, "end": v(42.45, -47.5) * mm, "construction": true});
            skLineSegment(sketch, "E27.3.11.0", {"start": v(46.68, -23.2) * mm, "end": v(49.41, -16.6) * mm});
            skCircle(sketch, "E27.6.11.0", {"center": v(39.55, -16.38) * mm, "radius": 2 * mm});
            skLineSegment(sketch, "E27.7.11.0", {"start": v(52.33, -15.4) * mm, "end": v(58.93, -18.13) * mm});
            skLineSegment(sketch, "E27.8.11.0", {"start": v(53.4, -22.12) * mm, "end": v(39.55, -16.38) * mm, "construction": true});
            skCircle(sketch, "E27.11.11.0", {"center": v(65.3, -13) * mm, "radius": 2 * mm});
            skCircle(sketch, "E27.13.11.0", {"center": v(55.36, -37) * mm, "radius": 2 * mm});
            skLineSegment(sketch, "E27.15.11.0", {"start": v(47.89, -26.11) * mm, "end": v(54.49, -28.85) * mm});
            skArc(sketch, "E27.18.11.0", {"start": v(57.4, -27.64) * mm, "mid": v(55.26, -26.6) * mm, "end": v(54.49, -28.85) * mm, "construction": true});
            skPoint(sketch, "E27.22.11.0", {"position": v(53.4, -22.12) * mm});
            skLineSegment(sketch, "E27.23.11.0", {"start": v(53.4, -22.12) * mm, "end": v(56.55, -29.7) * mm, "construction": true});
            skLineSegment(sketch, "E27.26.11.0", {"start": v(57.4, -27.64) * mm, "end": v(60.13, -21.04) * mm});
            skPoint(sketch, "E27.29.11.0", {"position": v(53.4, -22.12) * mm});
            skArc(sketch, "E27.30.11.0", {"start": v(52.33, -15.4) * mm, "mid": v(50.34, -14.7) * mm, "end": v(49.41, -16.6) * mm});
            skPoint(sketch, "E27.34.11.0", {"position": v(53.4, -22.12) * mm});
            skLineSegment(sketch, "E27.35.11.0", {"start": v(50.27, -14.54) * mm, "end": v(52.33, -15.4) * mm, "construction": true});
            skLineSegment(sketch, "E27.38.11.0", {"start": v(60.13, -21.04) * mm, "end": v(60.98, -18.98) * mm, "construction": true});
            skArc(sketch, "E27.41.11.0", {"start": v(60.13, -21.04) * mm, "mid": v(60.82, -19.05) * mm, "end": v(58.93, -18.13) * mm});
            skLineSegment(sketch, "E27.45.11.0", {"start": v(45.83, -25.26) * mm, "end": v(47.89, -26.11) * mm, "construction": true});
            skPoint(sketch, "E27.48.11.0", {"position": v(53.4, -22.12) * mm});
            skLineSegment(sketch, "E27.49.11.0", {"start": v(49.41, -16.6) * mm, "end": v(50.27, -14.54) * mm, "construction": true});
            skArc(sketch, "E27.52.11.0", {"start": v(46.68, -23.2) * mm, "mid": v(46, -25.2) * mm, "end": v(47.89, -26.11) * mm});
            skLineSegment(sketch, "E27.56.11.0", {"start": v(45.83, -25.26) * mm, "end": v(46.68, -23.2) * mm, "construction": true});
            skLineSegment(sketch, "E27.59.11.0", {"start": v(58.93, -18.13) * mm, "end": v(60.98, -18.98) * mm, "construction": true});
            skPoint(sketch, "E27.62.11.0", {"position": v(53.4, -22.12) * mm});
            skPoint(sketch, "E27.63.11.0", {"position": v(53.4, -22.12) * mm});
            skLineSegment(sketch, "E27.64.11.0", {"start": v(54.49, -28.85) * mm, "end": v(56.55, -29.7) * mm, "construction": true});
            skArc(sketch, "E27.67.11.0", {"start": v(54.49, -28.85) * mm, "mid": v(56.48, -29.53) * mm, "end": v(57.4, -27.64) * mm});
            skLineSegment(sketch, "E27.71.11.0", {"start": v(56.55, -29.7) * mm, "end": v(56.55, -29.5) * mm, "construction": true});
            skLineSegment(sketch, "E27.74.11.0", {"start": v(56.55, -29.7) * mm, "end": v(57.4, -27.64) * mm, "construction": true});
            skLineSegment(sketch, "E27.3.12.0", {"start": v(52, -3.57) * mm, "end": v(52, 3.57) * mm});
            skCircle(sketch, "E27.6.12.0", {"center": v(42.8, 0) * mm, "radius": 2 * mm});
            skLineSegment(sketch, "E27.7.12.0", {"start": v(54.24, 5.8) * mm, "end": v(61.38, 5.8) * mm});
            skLineSegment(sketch, "E27.8.12.0", {"start": v(57.8, 0) * mm, "end": v(42.8, 0) * mm, "construction": true});
            skCircle(sketch, "E27.11.12.0", {"center": v(65.3, 13) * mm, "radius": 2 * mm});
            skCircle(sketch, "E27.13.12.0", {"center": v(65.3, -13) * mm, "radius": 2 * mm});
            skLineSegment(sketch, "E27.15.12.0", {"start": v(54.24, -5.8) * mm, "end": v(61.38, -5.8) * mm});
            skArc(sketch, "E27.18.12.0", {"start": v(63.6, -3.57) * mm, "mid": v(61.23, -3.43) * mm, "end": v(61.38, -5.8) * mm, "construction": true});
            skPoint(sketch, "E27.22.12.0", {"position": v(57.8, 0) * mm});
            skLineSegment(sketch, "E27.23.12.0", {"start": v(57.8, 0) * mm, "end": v(63.6, -5.8) * mm, "construction": true});
            skLineSegment(sketch, "E27.26.12.0", {"start": v(63.6, -3.57) * mm, "end": v(63.6, 3.57) * mm});
            skPoint(sketch, "E27.29.12.0", {"position": v(57.8, 0) * mm});
            skArc(sketch, "E27.30.12.0", {"start": v(54.24, 5.8) * mm, "mid": v(52.13, 5.67) * mm, "end": v(52, 3.57) * mm});
            skPoint(sketch, "E27.34.12.0", {"position": v(57.8, 0) * mm});
            skLineSegment(sketch, "E27.35.12.0", {"start": v(52, 5.8) * mm, "end": v(54.24, 5.8) * mm, "construction": true});
            skLineSegment(sketch, "E27.38.12.0", {"start": v(63.6, 3.57) * mm, "end": v(63.6, 5.8) * mm, "construction": true});
            skArc(sketch, "E27.41.12.0", {"start": v(63.6, 3.57) * mm, "mid": v(63.48, 5.67) * mm, "end": v(61.38, 5.8) * mm});
            skLineSegment(sketch, "E27.45.12.0", {"start": v(52, -5.8) * mm, "end": v(54.24, -5.8) * mm, "construction": true});
            skPoint(sketch, "E27.48.12.0", {"position": v(57.8, 0) * mm});
            skLineSegment(sketch, "E27.49.12.0", {"start": v(52, 3.57) * mm, "end": v(52, 5.8) * mm, "construction": true});
            skArc(sketch, "E27.52.12.0", {"start": v(52, -3.57) * mm, "mid": v(52.13, -5.67) * mm, "end": v(54.24, -5.8) * mm});
            skLineSegment(sketch, "E27.56.12.0", {"start": v(52, -5.8) * mm, "end": v(52, -3.57) * mm, "construction": true});
            skLineSegment(sketch, "E27.59.12.0", {"start": v(61.38, 5.8) * mm, "end": v(63.6, 5.8) * mm, "construction": true});
            skPoint(sketch, "E27.62.12.0", {"position": v(57.8, 0) * mm});
            skPoint(sketch, "E27.63.12.0", {"position": v(57.8, 0) * mm});
            skLineSegment(sketch, "E27.64.12.0", {"start": v(61.38, -5.8) * mm, "end": v(63.6, -5.8) * mm, "construction": true});
            skArc(sketch, "E27.67.12.0", {"start": v(61.38, -5.8) * mm, "mid": v(63.48, -5.67) * mm, "end": v(63.6, -3.57) * mm});
            skLineSegment(sketch, "E27.71.12.0", {"start": v(63.6, -5.8) * mm, "end": v(63.54, -5.61) * mm, "construction": true});
            skLineSegment(sketch, "E27.74.12.0", {"start": v(63.6, -5.8) * mm, "end": v(63.6, -3.57) * mm, "construction": true});
            skLineSegment(sketch, "E27.3.13.0", {"start": v(49.41, 16.6) * mm, "end": v(46.68, 23.2) * mm});
            skCircle(sketch, "E27.6.13.0", {"center": v(39.55, 16.38) * mm, "radius": 2 * mm});
            skLineSegment(sketch, "E27.7.13.0", {"start": v(47.89, 26.11) * mm, "end": v(54.49, 28.85) * mm});
            skLineSegment(sketch, "E27.8.13.0", {"start": v(53.4, 22.12) * mm, "end": v(39.55, 16.38) * mm, "construction": true});
            skCircle(sketch, "E27.11.13.0", {"center": v(55.36, 37) * mm, "radius": 2 * mm});
            skCircle(sketch, "E27.13.13.0", {"center": v(65.3, 13) * mm, "radius": 2 * mm});
            skLineSegment(sketch, "E27.15.13.0", {"start": v(52.33, 15.4) * mm, "end": v(58.93, 18.13) * mm});
            skArc(sketch, "E27.18.13.0", {"start": v(60.13, 21.04) * mm, "mid": v(57.89, 20.27) * mm, "end": v(58.93, 18.13) * mm, "construction": true});
            skPoint(sketch, "E27.22.13.0", {"position": v(53.4, 22.12) * mm});
            skLineSegment(sketch, "E27.23.13.0", {"start": v(53.4, 22.12) * mm, "end": v(60.98, 18.98) * mm, "construction": true});
            skLineSegment(sketch, "E27.26.13.0", {"start": v(60.13, 21.04) * mm, "end": v(57.4, 27.64) * mm});
            skPoint(sketch, "E27.29.13.0", {"position": v(53.4, 22.12) * mm});
            skArc(sketch, "E27.30.13.0", {"start": v(47.89, 26.11) * mm, "mid": v(46, 25.2) * mm, "end": v(46.68, 23.2) * mm});
            skPoint(sketch, "E27.34.13.0", {"position": v(53.4, 22.12) * mm});
            skLineSegment(sketch, "E27.35.13.0", {"start": v(45.83, 25.26) * mm, "end": v(47.89, 26.11) * mm, "construction": true});
            skLineSegment(sketch, "E27.38.13.0", {"start": v(57.4, 27.64) * mm, "end": v(56.55, 29.7) * mm, "construction": true});
            skArc(sketch, "E27.41.13.0", {"start": v(57.4, 27.64) * mm, "mid": v(56.48, 29.53) * mm, "end": v(54.49, 28.85) * mm});
            skLineSegment(sketch, "E27.45.13.0", {"start": v(50.27, 14.54) * mm, "end": v(52.33, 15.4) * mm, "construction": true});
            skPoint(sketch, "E27.48.13.0", {"position": v(53.4, 22.12) * mm});
            skLineSegment(sketch, "E27.49.13.0", {"start": v(46.68, 23.2) * mm, "end": v(45.83, 25.26) * mm, "construction": true});
            skArc(sketch, "E27.52.13.0", {"start": v(49.41, 16.6) * mm, "mid": v(50.34, 14.7) * mm, "end": v(52.33, 15.4) * mm});
            skLineSegment(sketch, "E27.56.13.0", {"start": v(50.27, 14.54) * mm, "end": v(49.41, 16.6) * mm, "construction": true});
            skLineSegment(sketch, "E27.59.13.0", {"start": v(54.49, 28.85) * mm, "end": v(56.55, 29.7) * mm, "construction": true});
            skPoint(sketch, "E27.62.13.0", {"position": v(53.4, 22.12) * mm});
            skPoint(sketch, "E27.63.13.0", {"position": v(53.4, 22.12) * mm});
            skLineSegment(sketch, "E27.64.13.0", {"start": v(58.93, 18.13) * mm, "end": v(60.98, 18.98) * mm, "construction": true});
            skArc(sketch, "E27.67.13.0", {"start": v(58.93, 18.13) * mm, "mid": v(60.82, 19.05) * mm, "end": v(60.13, 21.04) * mm});
            skLineSegment(sketch, "E27.71.13.0", {"start": v(60.98, 18.98) * mm, "end": v(60.85, 19.13) * mm, "construction": true});
            skLineSegment(sketch, "E27.74.13.0", {"start": v(60.98, 18.98) * mm, "end": v(60.13, 21.04) * mm, "construction": true});
            skLineSegment(sketch, "E27.3.14.0", {"start": v(39.3, 34.25) * mm, "end": v(34.25, 39.3) * mm});
            skCircle(sketch, "E27.6.14.0", {"center": v(30.27, 30.27) * mm, "radius": 2 * mm});
            skLineSegment(sketch, "E27.7.14.0", {"start": v(34.25, 42.45) * mm, "end": v(39.3, 47.5) * mm});
            skLineSegment(sketch, "E27.8.14.0", {"start": v(40.88, 40.88) * mm, "end": v(30.27, 30.27) * mm, "construction": true});
            skCircle(sketch, "E27.11.14.0", {"center": v(37, 55.36) * mm, "radius": 2 * mm});
            skCircle(sketch, "E27.13.14.0", {"center": v(55.36, 37) * mm, "radius": 2 * mm});
            skLineSegment(sketch, "E27.15.14.0", {"start": v(42.45, 34.25) * mm, "end": v(47.5, 39.3) * mm});
            skArc(sketch, "E27.18.14.0", {"start": v(47.5, 42.45) * mm, "mid": v(45.72, 40.88) * mm, "end": v(47.5, 39.3) * mm, "construction": true});
            skPoint(sketch, "E27.22.14.0", {"position": v(40.88, 40.88) * mm});
            skLineSegment(sketch, "E27.23.14.0", {"start": v(40.88, 40.88) * mm, "end": v(49.08, 40.88) * mm, "construction": true});
            skLineSegment(sketch, "E27.26.14.0", {"start": v(47.5, 42.45) * mm, "end": v(42.45, 47.5) * mm});
            skPoint(sketch, "E27.29.14.0", {"position": v(40.88, 40.88) * mm});
            skArc(sketch, "E27.30.14.0", {"start": v(34.25, 42.45) * mm, "mid": v(32.85, 40.88) * mm, "end": v(34.25, 39.3) * mm});
            skPoint(sketch, "E27.34.14.0", {"position": v(40.88, 40.88) * mm});
            skLineSegment(sketch, "E27.35.14.0", {"start": v(32.67, 40.88) * mm, "end": v(34.25, 42.45) * mm, "construction": true});
            skLineSegment(sketch, "E27.38.14.0", {"start": v(42.45, 47.5) * mm, "end": v(40.88, 49.08) * mm, "construction": true});
            skArc(sketch, "E27.41.14.0", {"start": v(42.45, 47.5) * mm, "mid": v(40.88, 48.9) * mm, "end": v(39.3, 47.5) * mm});
            skLineSegment(sketch, "E27.45.14.0", {"start": v(40.88, 32.67) * mm, "end": v(42.45, 34.25) * mm, "construction": true});
            skPoint(sketch, "E27.48.14.0", {"position": v(40.88, 40.88) * mm});
            skLineSegment(sketch, "E27.49.14.0", {"start": v(34.25, 39.3) * mm, "end": v(32.67, 40.88) * mm, "construction": true});
            skArc(sketch, "E27.52.14.0", {"start": v(39.3, 34.25) * mm, "mid": v(40.88, 32.85) * mm, "end": v(42.45, 34.25) * mm});
            skLineSegment(sketch, "E27.56.14.0", {"start": v(40.88, 32.67) * mm, "end": v(39.3, 34.25) * mm, "construction": true});
            skLineSegment(sketch, "E27.59.14.0", {"start": v(39.3, 47.5) * mm, "end": v(40.88, 49.08) * mm, "construction": true});
            skPoint(sketch, "E27.62.14.0", {"position": v(40.88, 40.88) * mm});
            skPoint(sketch, "E27.63.14.0", {"position": v(40.88, 40.88) * mm});
            skLineSegment(sketch, "E27.64.14.0", {"start": v(47.5, 39.3) * mm, "end": v(49.08, 40.88) * mm, "construction": true});
            skArc(sketch, "E27.67.14.0", {"start": v(47.5, 39.3) * mm, "mid": v(48.9, 40.88) * mm, "end": v(47.5, 42.45) * mm});
            skLineSegment(sketch, "E27.71.14.0", {"start": v(49.08, 40.88) * mm, "end": v(48.9, 40.96) * mm, "construction": true});
            skLineSegment(sketch, "E27.74.14.0", {"start": v(49.08, 40.88) * mm, "end": v(47.5, 42.45) * mm, "construction": true});
            skLineSegment(sketch, "E27.3.15.0", {"start": v(23.2, 46.68) * mm, "end": v(16.6, 49.41) * mm});
            skCircle(sketch, "E27.6.15.0", {"center": v(16.38, 39.55) * mm, "radius": 2 * mm});
            skLineSegment(sketch, "E27.7.15.0", {"start": v(15.4, 52.33) * mm, "end": v(18.13, 58.93) * mm});
            skLineSegment(sketch, "E27.8.15.0", {"start": v(22.12, 53.4) * mm, "end": v(16.38, 39.55) * mm, "construction": true});
            skCircle(sketch, "E27.13.15.0", {"center": v(37, 55.36) * mm, "radius": 2 * mm});
            skLineSegment(sketch, "E27.15.15.0", {"start": v(26.11, 47.89) * mm, "end": v(28.85, 54.49) * mm});
            skArc(sketch, "E27.18.15.0", {"start": v(27.64, 57.4) * mm, "mid": v(26.6, 55.26) * mm, "end": v(28.85, 54.49) * mm, "construction": true});
            skPoint(sketch, "E27.22.15.0", {"position": v(22.12, 53.4) * mm});
            skLineSegment(sketch, "E27.23.15.0", {"start": v(22.12, 53.4) * mm, "end": v(29.7, 56.55) * mm, "construction": true});
            skLineSegment(sketch, "E27.26.15.0", {"start": v(27.64, 57.4) * mm, "end": v(21.04, 60.13) * mm});
            skPoint(sketch, "E27.29.15.0", {"position": v(22.12, 53.4) * mm});
            skArc(sketch, "E27.30.15.0", {"start": v(15.4, 52.33) * mm, "mid": v(14.7, 50.34) * mm, "end": v(16.6, 49.41) * mm});
            skPoint(sketch, "E27.34.15.0", {"position": v(22.12, 53.4) * mm});
            skLineSegment(sketch, "E27.35.15.0", {"start": v(14.54, 50.27) * mm, "end": v(15.4, 52.33) * mm, "construction": true});
            skLineSegment(sketch, "E27.38.15.0", {"start": v(21.04, 60.13) * mm, "end": v(18.98, 60.98) * mm, "construction": true});
            skArc(sketch, "E27.41.15.0", {"start": v(21.04, 60.13) * mm, "mid": v(19.05, 60.82) * mm, "end": v(18.13, 58.93) * mm});
            skLineSegment(sketch, "E27.45.15.0", {"start": v(25.26, 45.83) * mm, "end": v(26.11, 47.89) * mm, "construction": true});
            skPoint(sketch, "E27.48.15.0", {"position": v(22.12, 53.4) * mm});
            skLineSegment(sketch, "E27.49.15.0", {"start": v(16.6, 49.41) * mm, "end": v(14.54, 50.27) * mm, "construction": true});
            skArc(sketch, "E27.52.15.0", {"start": v(23.2, 46.68) * mm, "mid": v(25.2, 46) * mm, "end": v(26.11, 47.89) * mm});
            skLineSegment(sketch, "E27.56.15.0", {"start": v(25.26, 45.83) * mm, "end": v(23.2, 46.68) * mm, "construction": true});
            skLineSegment(sketch, "E27.59.15.0", {"start": v(18.13, 58.93) * mm, "end": v(18.98, 60.98) * mm, "construction": true});
            skPoint(sketch, "E27.62.15.0", {"position": v(22.12, 53.4) * mm});
            skPoint(sketch, "E27.63.15.0", {"position": v(22.12, 53.4) * mm});
            skLineSegment(sketch, "E27.64.15.0", {"start": v(28.85, 54.49) * mm, "end": v(29.7, 56.55) * mm, "construction": true});
            skArc(sketch, "E27.67.15.0", {"start": v(28.85, 54.49) * mm, "mid": v(29.53, 56.48) * mm, "end": v(27.64, 57.4) * mm});
            skLineSegment(sketch, "E27.71.15.0", {"start": v(29.7, 56.55) * mm, "end": v(29.5, 56.55) * mm, "construction": true});
            skLineSegment(sketch, "E27.74.15.0", {"start": v(29.7, 56.55) * mm, "end": v(27.64, 57.4) * mm, "construction": true});
            skLineSegment(sketch, "E28.bottom", {"start": v(-2, 63.6) * mm, "end": v(2, 63.6) * mm});
            skLineSegment(sketch, "E28.top", {"start": v(-2, 73.6) * mm, "end": v(2, 73.6) * mm});
            skLineSegment(sketch, "E28.left", {"start": v(-2, 63.6) * mm, "end": v(-2, 73.6) * mm});
            skLineSegment(sketch, "E28.right", {"start": v(2, 63.6) * mm, "end": v(2, 73.6) * mm});
            skPoint(sketch, "E29", {"position": v(0, 73.6) * mm});
            skPoint(sketch, "E30", {"position": v(0, 63.6) * mm});
            skLineSegment(sketch, "E31.1.0", {"start": v(-26.19, 58) * mm, "end": v(-30.02, 67.24) * mm});
            skLineSegment(sketch, "E31.1.1", {"start": v(-30.02, 67.24) * mm, "end": v(-26.32, 68.77) * mm});
            skLineSegment(sketch, "E31.1.2", {"start": v(-22.5, 59.53) * mm, "end": v(-26.32, 68.77) * mm});
            skLineSegment(sketch, "E31.2.0", {"start": v(-46.4, 43.56) * mm, "end": v(-53.46, 50.63) * mm});
            skLineSegment(sketch, "E31.2.1", {"start": v(-53.46, 50.63) * mm, "end": v(-50.63, 53.46) * mm});
            skLineSegment(sketch, "E31.2.2", {"start": v(-43.56, 46.4) * mm, "end": v(-50.63, 53.46) * mm});
            skLineSegment(sketch, "E31.3.0", {"start": v(-59.53, 22.5) * mm, "end": v(-68.77, 26.32) * mm});
            skLineSegment(sketch, "E31.3.1", {"start": v(-68.77, 26.32) * mm, "end": v(-67.24, 30.02) * mm});
            skLineSegment(sketch, "E31.3.2", {"start": v(-58, 26.19) * mm, "end": v(-67.24, 30.02) * mm});
            skLineSegment(sketch, "E31.4.0", {"start": v(-63.6, -2) * mm, "end": v(-73.6, -2) * mm});
            skLineSegment(sketch, "E31.4.1", {"start": v(-73.6, -2) * mm, "end": v(-73.6, 2) * mm});
            skLineSegment(sketch, "E31.4.2", {"start": v(-63.6, 2) * mm, "end": v(-73.6, 2) * mm});
            skLineSegment(sketch, "E31.5.0", {"start": v(-58, -26.19) * mm, "end": v(-67.24, -30.02) * mm});
            skLineSegment(sketch, "E31.5.1", {"start": v(-67.24, -30.02) * mm, "end": v(-68.77, -26.32) * mm});
            skLineSegment(sketch, "E31.5.2", {"start": v(-59.53, -22.5) * mm, "end": v(-68.77, -26.32) * mm});
            skLineSegment(sketch, "E31.6.0", {"start": v(-43.56, -46.4) * mm, "end": v(-50.63, -53.46) * mm});
            skLineSegment(sketch, "E31.6.1", {"start": v(-50.63, -53.46) * mm, "end": v(-53.46, -50.63) * mm});
            skLineSegment(sketch, "E31.6.2", {"start": v(-46.4, -43.56) * mm, "end": v(-53.46, -50.63) * mm});
            skLineSegment(sketch, "E31.7.0", {"start": v(-22.5, -59.53) * mm, "end": v(-26.32, -68.77) * mm});
            skLineSegment(sketch, "E31.7.1", {"start": v(-26.32, -68.77) * mm, "end": v(-30.02, -67.24) * mm});
            skLineSegment(sketch, "E31.7.2", {"start": v(-26.19, -58) * mm, "end": v(-30.02, -67.24) * mm});
            skLineSegment(sketch, "E31.8.0", {"start": v(2, -63.6) * mm, "end": v(2, -73.6) * mm});
            skLineSegment(sketch, "E31.8.1", {"start": v(2, -73.6) * mm, "end": v(-2, -73.6) * mm});
            skLineSegment(sketch, "E31.8.2", {"start": v(-2, -63.6) * mm, "end": v(-2, -73.6) * mm});
            skLineSegment(sketch, "E31.9.0", {"start": v(26.19, -58) * mm, "end": v(30.02, -67.24) * mm});
            skLineSegment(sketch, "E31.9.1", {"start": v(30.02, -67.24) * mm, "end": v(26.32, -68.77) * mm});
            skLineSegment(sketch, "E31.9.2", {"start": v(22.5, -59.53) * mm, "end": v(26.32, -68.77) * mm});
            skLineSegment(sketch, "E31.10.0", {"start": v(46.4, -43.56) * mm, "end": v(53.46, -50.63) * mm});
            skLineSegment(sketch, "E31.10.1", {"start": v(53.46, -50.63) * mm, "end": v(50.63, -53.46) * mm});
            skLineSegment(sketch, "E31.10.2", {"start": v(43.56, -46.4) * mm, "end": v(50.63, -53.46) * mm});
            skLineSegment(sketch, "E31.11.0", {"start": v(59.53, -22.5) * mm, "end": v(68.77, -26.32) * mm});
            skLineSegment(sketch, "E31.11.1", {"start": v(68.77, -26.32) * mm, "end": v(67.24, -30.02) * mm});
            skLineSegment(sketch, "E31.11.2", {"start": v(58, -26.19) * mm, "end": v(67.24, -30.02) * mm});
            skLineSegment(sketch, "E31.12.0", {"start": v(63.6, 2) * mm, "end": v(73.6, 2) * mm});
            skLineSegment(sketch, "E31.12.1", {"start": v(73.6, 2) * mm, "end": v(73.6, -2) * mm});
            skLineSegment(sketch, "E31.12.2", {"start": v(63.6, -2) * mm, "end": v(73.6, -2) * mm});
            skLineSegment(sketch, "E31.13.0", {"start": v(58, 26.19) * mm, "end": v(67.24, 30.02) * mm});
            skLineSegment(sketch, "E31.13.1", {"start": v(67.24, 30.02) * mm, "end": v(68.77, 26.32) * mm});
            skLineSegment(sketch, "E31.13.2", {"start": v(59.53, 22.5) * mm, "end": v(68.77, 26.32) * mm});
            skLineSegment(sketch, "E31.14.0", {"start": v(43.56, 46.4) * mm, "end": v(50.63, 53.46) * mm});
            skLineSegment(sketch, "E31.14.1", {"start": v(50.63, 53.46) * mm, "end": v(53.46, 50.63) * mm});
            skLineSegment(sketch, "E31.14.2", {"start": v(46.4, 43.56) * mm, "end": v(53.46, 50.63) * mm});
            skLineSegment(sketch, "E31.15.0", {"start": v(22.5, 59.53) * mm, "end": v(26.32, 68.77) * mm});
            skLineSegment(sketch, "E31.15.1", {"start": v(26.32, 68.77) * mm, "end": v(30.02, 67.24) * mm});
            skLineSegment(sketch, "E31.15.2", {"start": v(26.19, 58) * mm, "end": v(30.02, 67.24) * mm});
            skLineSegment(sketch, "E32.bottom", {"start": v(5.25, 19.75) * mm, "end": v(3.02, 19.75) * mm, "construction": true});
            skLineSegment(sketch, "E32.top", {"start": v(5.25, 30.25) * mm, "end": v(3.02, 30.25) * mm, "construction": true});
            skLineSegment(sketch, "E32.left", {"start": v(5.25, 19.75) * mm, "end": v(5.25, 19.75) * mm});
            skLineSegment(sketch, "E32.right", {"start": v(-5.25, 19.75) * mm, "end": v(-5.25, 21.98) * mm, "construction": true});
            skPoint(sketch, "E32.middle", {"position": v(0, 25) * mm});
            skLineSegment(sketch, "E33", {"start": v(0, 25) * mm, "end": v(5.25, 30.25) * mm, "construction": true});
            skLineSegment(sketch, "E34", {"start": v(5.25, 30.25) * mm, "end": v(5.4, 30.4) * mm, "construction": true});
            skArc(sketch, "E35", {"start": v(5.25, 28.02) * mm, "mid": v(5.4, 30.4) * mm, "end": v(3.02, 30.25) * mm});
            skArc(sketch, "E36", {"start": v(3.02, 30.25) * mm, "mid": v(3.15, 28.15) * mm, "end": v(5.25, 28.02) * mm, "construction": true});
            skLineSegment(sketch, "E37", {"start": v(5.25, 28.02) * mm, "end": v(5.25, 30.25) * mm, "construction": true});
            skLineSegment(sketch, "E38", {"start": v(5.25, 19.75) * mm, "end": v(5.25, 21.98) * mm, "construction": true});
            skLineSegment(sketch, "E39", {"start": v(3.02, 30.25) * mm, "end": v(3.02, 30.25) * mm});
            skLineSegment(sketch, "E40", {"start": v(-5.25, 30.25) * mm, "end": v(-5.25, 30.25) * mm});
            skArc(sketch, "E41.1.0", {"start": v(-3.02, 30.25) * mm, "mid": v(-5.4, 30.4) * mm, "end": v(-5.25, 28.02) * mm});
            skArc(sketch, "E41.2.0", {"start": v(-5.25, 21.98) * mm, "mid": v(-5.4, 19.6) * mm, "end": v(-3.02, 19.75) * mm});
            skArc(sketch, "E42.2.3.0", {"start": v(3.02, 19.75) * mm, "mid": v(5.4, 19.6) * mm, "end": v(5.25, 21.98) * mm});
            skLineSegment(sketch, "E43", {"start": v(-5.25, 28.02) * mm, "end": v(-5.25, 30.25) * mm, "construction": true});
            skLineSegment(sketch, "E44", {"start": v(-5.25, 21.98) * mm, "end": v(-5.25, 28.02) * mm});
            skLineSegment(sketch, "E45", {"start": v(-3.02, 19.75) * mm, "end": v(-5.25, 19.75) * mm, "construction": true});
            skLineSegment(sketch, "E46", {"start": v(3.02, 19.75) * mm, "end": v(-3.02, 19.75) * mm});
            skLineSegment(sketch, "E47", {"start": v(3.02, 30.25) * mm, "end": v(-3.02, 30.25) * mm});
            skLineSegment(sketch, "E48", {"start": v(-3.02, 30.25) * mm, "end": v(-5.25, 30.25) * mm, "construction": true});
            skLineSegment(sketch, "E49", {"start": v(5.25, 21.98) * mm, "end": v(5.25, 28.02) * mm});
            skLineSegment(sketch, "E50", {"start": v(5.25, 28.02) * mm, "end": v(5.25, 28.02) * mm});
            skLineSegment(sketch, "E51.bottom", {"start": v(-2, 30.25) * mm, "end": v(2, 30.25) * mm});
            skPoint(sketch, "E52", {"position": v(0, 30.25) * mm});
            skLineSegment(sketch, "E53", {"start": v(0, 42.8) * mm, "end": v(0, 0) * mm, "construction": true});
            skLineSegment(sketch, "E54.1.0", {"start": v(-21.98, -5.25) * mm, "end": v(-28.02, -5.25) * mm});
            skLineSegment(sketch, "E54.1.1", {"start": v(-19.75, -5.25) * mm, "end": v(-21.98, -5.25) * mm, "construction": true});
            skPoint(sketch, "E54.1.2", {"position": v(-30.25, 0) * mm});
            skArc(sketch, "E54.1.3", {"start": v(-30.25, -3.02) * mm, "mid": v(-30.4, -5.4) * mm, "end": v(-28.02, -5.25) * mm});
            skArc(sketch, "E54.1.4", {"start": v(-21.98, -5.25) * mm, "mid": v(-19.6, -5.4) * mm, "end": v(-19.75, -3.02) * mm});
            skLineSegment(sketch, "E54.1.5", {"start": v(-28.02, -5.25) * mm, "end": v(-30.25, -5.25) * mm, "construction": true});
            skLineSegment(sketch, "E54.1.6", {"start": v(-19.75, -3.02) * mm, "end": v(-19.75, -5.25) * mm, "construction": true});
            skLineSegment(sketch, "E54.1.7", {"start": v(-19.75, 3.02) * mm, "end": v(-19.75, -3.02) * mm});
            skLineSegment(sketch, "E54.1.8", {"start": v(-30.25, -3.02) * mm, "end": v(-30.25, -5.25) * mm, "construction": true});
            skLineSegment(sketch, "E54.1.9", {"start": v(-21.98, 5.25) * mm, "end": v(-28.02, 5.25) * mm});
            skArc(sketch, "E54.1.11", {"start": v(-28.02, 5.25) * mm, "mid": v(-30.4, 5.4) * mm, "end": v(-30.25, 3.02) * mm});
            skPoint(sketch, "E54.1.12", {"position": v(-25, 0) * mm});
            skArc(sketch, "E54.1.13", {"start": v(-30.25, 3.02) * mm, "mid": v(-28.15, 3.15) * mm, "end": v(-28.02, 5.25) * mm, "construction": true});
            skLineSegment(sketch, "E54.1.14", {"start": v(-28.02, 5.25) * mm, "end": v(-30.25, 5.25) * mm, "construction": true});
            skArc(sketch, "E54.1.15", {"start": v(-19.75, 3.02) * mm, "mid": v(-19.6, 5.4) * mm, "end": v(-21.98, 5.25) * mm});
            skLineSegment(sketch, "E54.1.16", {"start": v(-19.75, 5.25) * mm, "end": v(-19.75, 3.02) * mm, "construction": true});
            skLineSegment(sketch, "E54.1.17", {"start": v(-30.25, 3.02) * mm, "end": v(-30.25, -3.02) * mm});
            skLineSegment(sketch, "E54.1.18", {"start": v(-30.25, 5.25) * mm, "end": v(-30.25, 3.02) * mm, "construction": true});
            skLineSegment(sketch, "E54.1.19", {"start": v(-30.25, -2) * mm, "end": v(-30.25, 2) * mm});
            skPoint(sketch, "E54.1.20", {"position": v(-25, 0) * mm});
            skLineSegment(sketch, "E54.1.21", {"start": v(-19.75, 5.25) * mm, "end": v(-21.98, 5.25) * mm, "construction": true});
            skPoint(sketch, "E54.1.22", {"position": v(-25, 0) * mm});
            skPoint(sketch, "E54.1.23", {"position": v(-25, 0) * mm});
            skPoint(sketch, "E54.1.24", {"position": v(-25, 0) * mm});
            skLineSegment(sketch, "E54.1.25", {"start": v(-30.25, 5.25) * mm, "end": v(-30.4, 5.4) * mm, "construction": true});
            skPoint(sketch, "E54.1.26", {"position": v(-25, 0) * mm});
            skLineSegment(sketch, "E54.2.0", {"start": v(5.25, -21.98) * mm, "end": v(5.25, -28.02) * mm});
            skLineSegment(sketch, "E54.2.1", {"start": v(5.25, -19.75) * mm, "end": v(5.25, -21.98) * mm, "construction": true});
            skPoint(sketch, "E54.2.2", {"position": v(0, -30.25) * mm});
            skArc(sketch, "E54.2.3", {"start": v(3.02, -30.25) * mm, "mid": v(5.4, -30.4) * mm, "end": v(5.25, -28.02) * mm});
            skArc(sketch, "E54.2.4", {"start": v(5.25, -21.98) * mm, "mid": v(5.4, -19.6) * mm, "end": v(3.02, -19.75) * mm});
            skLineSegment(sketch, "E54.2.5", {"start": v(5.25, -28.02) * mm, "end": v(5.25, -30.25) * mm, "construction": true});
            skLineSegment(sketch, "E54.2.6", {"start": v(3.02, -19.75) * mm, "end": v(5.25, -19.75) * mm, "construction": true});
            skLineSegment(sketch, "E54.2.7", {"start": v(-3.02, -19.75) * mm, "end": v(3.02, -19.75) * mm});
            skLineSegment(sketch, "E54.2.8", {"start": v(3.02, -30.25) * mm, "end": v(5.25, -30.25) * mm, "construction": true});
            skLineSegment(sketch, "E54.2.9", {"start": v(-5.25, -21.98) * mm, "end": v(-5.25, -28.02) * mm});
            skLineSegment(sketch, "E54.2.10", {"start": v(0, -25) * mm, "end": v(-5.25, -30.25) * mm, "construction": true});
            skArc(sketch, "E54.2.11", {"start": v(-5.25, -28.02) * mm, "mid": v(-5.4, -30.4) * mm, "end": v(-3.02, -30.25) * mm});
            skPoint(sketch, "E54.2.12", {"position": v(0, -25) * mm});
            skArc(sketch, "E54.2.13", {"start": v(-3.02, -30.25) * mm, "mid": v(-3.15, -28.15) * mm, "end": v(-5.25, -28.02) * mm, "construction": true});
            skLineSegment(sketch, "E54.2.14", {"start": v(-5.25, -28.02) * mm, "end": v(-5.25, -30.25) * mm, "construction": true});
            skArc(sketch, "E54.2.15", {"start": v(-3.02, -19.75) * mm, "mid": v(-5.4, -19.6) * mm, "end": v(-5.25, -21.98) * mm});
            skLineSegment(sketch, "E54.2.16", {"start": v(-5.25, -19.75) * mm, "end": v(-3.02, -19.75) * mm, "construction": true});
            skLineSegment(sketch, "E54.2.17", {"start": v(-3.02, -30.25) * mm, "end": v(3.02, -30.25) * mm});
            skLineSegment(sketch, "E54.2.18", {"start": v(-5.25, -30.25) * mm, "end": v(-3.02, -30.25) * mm, "construction": true});
            skLineSegment(sketch, "E54.2.19", {"start": v(2, -30.25) * mm, "end": v(-2, -30.25) * mm});
            skPoint(sketch, "E54.2.20", {"position": v(0, -25) * mm});
            skLineSegment(sketch, "E54.2.21", {"start": v(-5.25, -19.75) * mm, "end": v(-5.25, -21.98) * mm, "construction": true});
            skPoint(sketch, "E54.2.22", {"position": v(0, -25) * mm});
            skPoint(sketch, "E54.2.23", {"position": v(0, -25) * mm});
            skPoint(sketch, "E54.2.24", {"position": v(0, -25) * mm});
            skLineSegment(sketch, "E54.2.25", {"start": v(-5.25, -30.25) * mm, "end": v(-5.4, -30.4) * mm, "construction": true});
            skPoint(sketch, "E54.2.26", {"position": v(0, -25) * mm});
            skLineSegment(sketch, "E55.3.3.0", {"start": v(19.75, 5.25) * mm, "end": v(21.98, 5.25) * mm, "construction": true});
            skLineSegment(sketch, "E55.4.3.0", {"start": v(21.98, 5.25) * mm, "end": v(28.02, 5.25) * mm});
            skPoint(sketch, "E55.6.3.0", {"position": v(30.25, 0) * mm});
            skArc(sketch, "E55.7.3.0", {"start": v(30.25, 3.02) * mm, "mid": v(30.4, 5.4) * mm, "end": v(28.02, 5.25) * mm});
            skArc(sketch, "E55.11.3.0", {"start": v(21.98, 5.25) * mm, "mid": v(19.6, 5.4) * mm, "end": v(19.75, 3.02) * mm});
            skLineSegment(sketch, "E55.15.3.0", {"start": v(28.02, 5.25) * mm, "end": v(30.25, 5.25) * mm, "construction": true});
            skLineSegment(sketch, "E55.18.3.0", {"start": v(19.75, 3.02) * mm, "end": v(19.75, 5.25) * mm, "construction": true});
            skLineSegment(sketch, "E55.21.3.0", {"start": v(19.75, -3.02) * mm, "end": v(19.75, 3.02) * mm});
            skLineSegment(sketch, "E55.24.3.0", {"start": v(30.25, 3.02) * mm, "end": v(30.25, 5.25) * mm, "construction": true});
            skLineSegment(sketch, "E55.27.3.0", {"start": v(21.98, -5.25) * mm, "end": v(28.02, -5.25) * mm});
            skLineSegment(sketch, "E55.30.3.0", {"start": v(25, 0) * mm, "end": v(30.25, -5.25) * mm, "construction": true});
            skArc(sketch, "E55.33.3.0", {"start": v(28.02, -5.25) * mm, "mid": v(30.4, -5.4) * mm, "end": v(30.25, -3.02) * mm});
            skPoint(sketch, "E55.37.3.0", {"position": v(25, 0) * mm});
            skArc(sketch, "E55.38.3.0", {"start": v(30.25, -3.02) * mm, "mid": v(28.15, -3.15) * mm, "end": v(28.02, -5.25) * mm, "construction": true});
            skLineSegment(sketch, "E55.42.3.0", {"start": v(28.02, -5.25) * mm, "end": v(30.25, -5.25) * mm, "construction": true});
            skArc(sketch, "E55.45.3.0", {"start": v(19.75, -3.02) * mm, "mid": v(19.6, -5.4) * mm, "end": v(21.98, -5.25) * mm});
            skLineSegment(sketch, "E55.49.3.0", {"start": v(19.75, -5.25) * mm, "end": v(19.75, -3.02) * mm, "construction": true});
            skLineSegment(sketch, "E55.52.3.0", {"start": v(30.25, -3.02) * mm, "end": v(30.25, 3.02) * mm});
            skLineSegment(sketch, "E55.55.3.0", {"start": v(30.25, -5.25) * mm, "end": v(30.25, -3.02) * mm, "construction": true});
            skLineSegment(sketch, "E55.58.3.0", {"start": v(30.25, 2) * mm, "end": v(30.25, -2) * mm});
            skPoint(sketch, "E55.61.3.0", {"position": v(25, 0) * mm});
            skLineSegment(sketch, "E55.62.3.0", {"start": v(19.75, -5.25) * mm, "end": v(21.98, -5.25) * mm, "construction": true});
            skPoint(sketch, "E55.65.3.0", {"position": v(25, 0) * mm});
            skPoint(sketch, "E55.66.3.0", {"position": v(25, 0) * mm});
            skPoint(sketch, "E55.67.3.0", {"position": v(25, 0) * mm});
            skLineSegment(sketch, "E55.68.3.0", {"start": v(30.25, -5.25) * mm, "end": v(30.4, -5.4) * mm, "construction": true});
            skPoint(sketch, "E55.71.3.0", {"position": v(25, 0) * mm});
            skSolve(sketch);
        }
        {
            var Q0;
            Q0=qSketchRegion(id+"F0",true);
            extrude(context, id + "F1", {"entities" : qUnion([Q0]), "depth" : 1 * mm});
        }
    });
